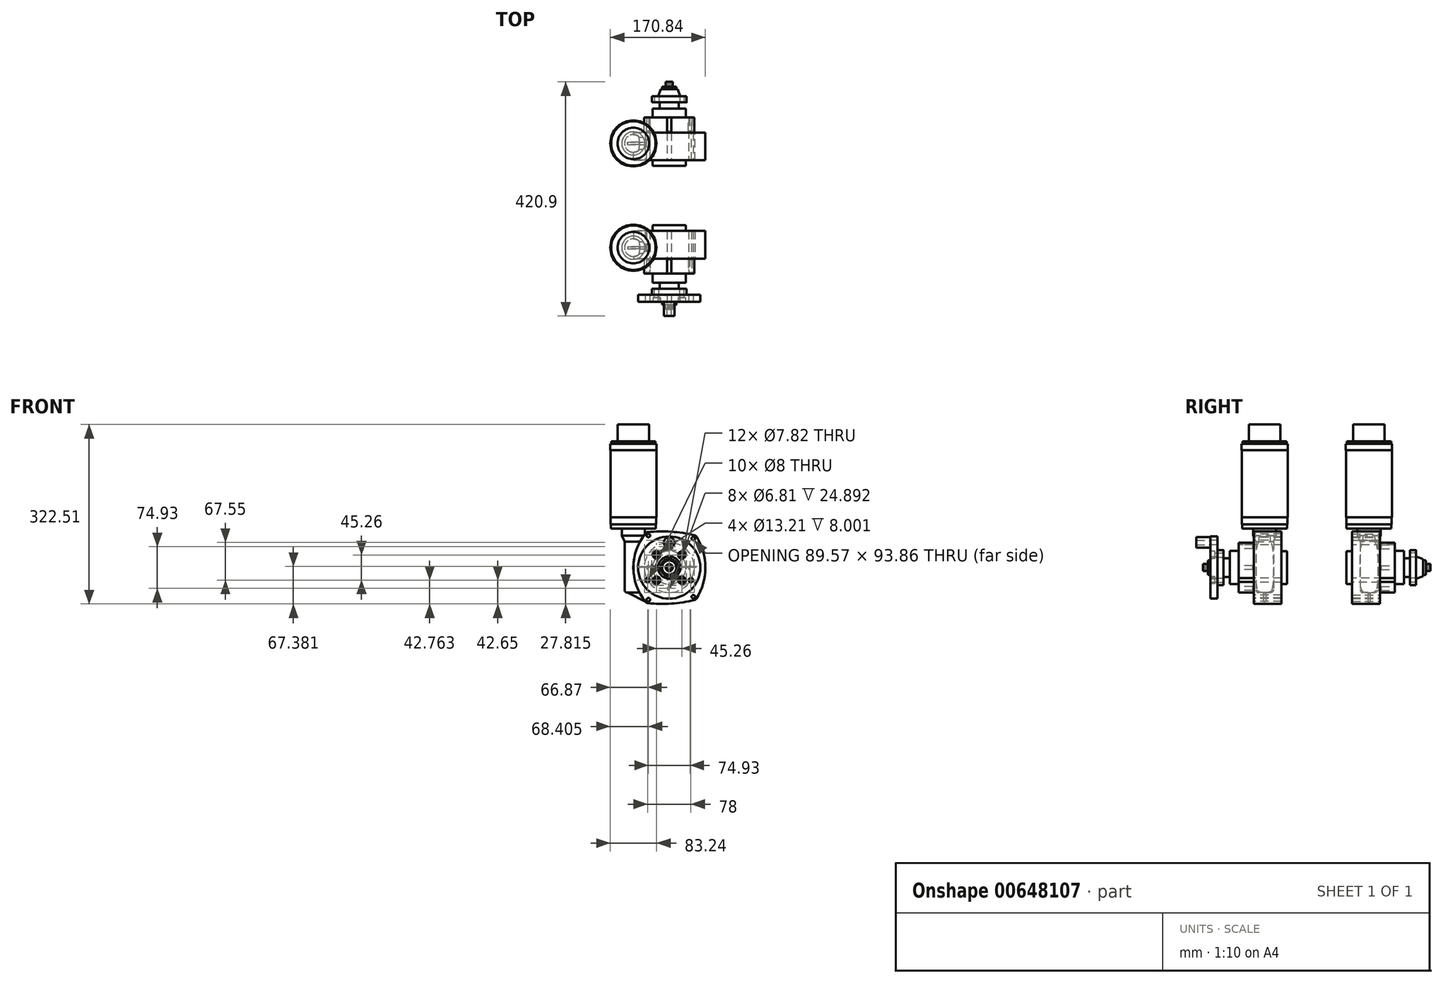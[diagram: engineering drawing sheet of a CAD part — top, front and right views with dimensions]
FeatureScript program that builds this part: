
annotation { "Feature Type Name" : "Feature", "Feature Type Description" : "" }
export const myFeature = defineFeature(function(context is Context, id is Id, definition is map)
    precondition{}
    {
        {
            var Q0;
            Q0=qCreatedBy(makeId("Front.planeOp"),FACE);
            var sketch = newSketch(context, id + "F0", { "sketchPlane" : qUnion([Q0])});
            skCircle(sketch, "E0", {"center": v(0, 0) * mm, "radius": 29.84 * mm});
            skSolve(sketch);
        }
        {
            var Q0;
            Q0 = qSketchRegion(id + "F0", true);
            extrude(context, id + "F1", {"entities" : qUnion([Q0]), "depth" : 16.13 * mm, "offsetDistance" : 25.4 * mm});
        }
        {
            var Q0;
            Q0=makeQuery(id+"F1.opExtrude","CAP_FACE",FACE,{"disambiguationData":[OSD([sQuery(id+"F0.wireOp",EDGE,"E0")])],"isStart":false});
            var sketch = newSketch(context, id + "F2", { "sketchPlane" : qUnion([Q0])});
            skCircle(sketch, "E1", {"center": v(0, 0) * mm, "radius": 44.83 * mm});
            skSolve(sketch);
        }
        {
            var Q0;
            Q0 = qSketchRegion(id + "F2", true);
            extrude(context, id + "F3", {"entities" : qUnion([Q0]), "operationType" : NewBodyOperationType.ADD, "depth" : 27.1 * mm, "offsetDistance" : 25.4 * mm});
        }
        {
            var Q0;
            Q0=makeQuery(id+"F3.opExtrude","CAP_FACE",FACE,{"disambiguationData":[OSD([sQuery(id+"F2.wireOp",EDGE,"E1")])],"isStart":true});
            var sketch = newSketch(context, id + "F4", { "sketchPlane" : qUnion([Q0])});
            skCircle(sketch, "E2", {"center": v(0, 37.47) * mm, "radius": 3.4 * mm});
            skCircle(sketch, "E3.1.0", {"center": v(-37.47, 0) * mm, "radius": 3.4 * mm});
            skCircle(sketch, "E3.2.0", {"center": v(0, -37.47) * mm, "radius": 3.4 * mm});
            skCircle(sketch, "E3.3.0", {"center": v(37.47, 0) * mm, "radius": 3.4 * mm});
            skPoint(sketch, "E3.center", {"position": v(0, 0) * mm});
            skSolve(sketch);
        }
        {
            var Q0;
            Q0 = qSketchRegion(id + "F4", true);
            extrude(context, id + "F5", {"entities" : qUnion([Q0]), "operationType" : NewBodyOperationType.REMOVE, "oppositeDirection" : true, "depth" : 24.9 * mm, "offsetDistance" : 25.4 * mm});
        }
        {
            var Q0;
            Q0=makeQuery(id+"F3.opExtrude","CAP_FACE",FACE,{"disambiguationData":[OSD([sQuery(id+"F2.wireOp",EDGE,"E1")])],"isStart":false});
            var sketch = newSketch(context, id + "F6", { "sketchPlane" : qUnion([Q0])});
            skCircle(sketch, "E4.0", {"center": v(0, 0) * mm, "radius": 44.83 * mm, "construction": true});
            skCircle(sketch, "E5", {"center": v(43.42, -52.43) * mm, "radius": 3.18 * mm});
            skCircle(sketch, "E6", {"center": v(43.42, 52.43) * mm, "radius": 3.18 * mm});
            skLineSegment(sketch, "E7", {"start": v(43.42, -52.43) * mm, "end": v(43.42, 52.43) * mm, "construction": true});
            skCircle(sketch, "E8", {"center": v(-37.44, 57.66) * mm, "radius": 3.18 * mm});
            skCircle(sketch, "E9", {"center": v(-37.44, -57.66) * mm, "radius": 3.18 * mm});
            skLineSegment(sketch, "E10", {"start": v(43.42, 52.43) * mm, "end": v(-37.44, 57.66) * mm, "construction": true});
            skLineSegment(sketch, "E11", {"start": v(-37.44, 57.66) * mm, "end": v(-37.44, -57.66) * mm, "construction": true});
            skLineSegment(sketch, "E12", {"start": v(0, 0) * mm, "end": v(47.8, 57.7) * mm, "construction": true});
            skLineSegment(sketch, "E13", {"start": v(0, 0) * mm, "end": v(-41.17, 63.4) * mm, "construction": true});
            skLineSegment(sketch, "E14", {"start": v(0, 0) * mm, "end": v(47.8, -57.7) * mm, "construction": true});
            skLineSegment(sketch, "E15", {"start": v(0, 0) * mm, "end": v(-41.17, -63.4) * mm, "construction": true});
            skArc(sketch, "E16", {"start": v(49.19, -55.51) * mm, "mid": v(64.97, -0.03) * mm, "end": v(49.22, 55.46) * mm});
            skArc(sketch, "E17", {"start": v(-42.88, 61.34) * mm, "mid": v(-64.47, -0.03) * mm, "end": v(-42.84, -61.4) * mm});
            skArc(sketch, "E18", {"start": v(45.26, 58.31) * mm, "mid": v(3.57, 64.45) * mm, "end": v(-38.56, 63.69) * mm});
            skArc(sketch, "E19", {"start": v(-38.62, -63.72) * mm, "mid": v(3.6, -64.8) * mm, "end": v(45.32, -58.34) * mm});
            skPoint(sketch, "E20.visualSharp", {"position": v(47.8, 57.7) * mm});
            skArc(sketch, "E20.filletArc", {"start": v(49.22, 55.46) * mm, "mid": v(47.52, 57.28) * mm, "end": v(45.26, 58.31) * mm});
            skPoint(sketch, "E21.visualSharp", {"position": v(47.8, -57.7) * mm});
            skArc(sketch, "E21.filletArc", {"start": v(45.32, -58.34) * mm, "mid": v(47.53, -57.3) * mm, "end": v(49.19, -55.51) * mm});
            skPoint(sketch, "E22.visualSharp", {"position": v(-41.17, -63.4) * mm});
            skArc(sketch, "E22.filletArc", {"start": v(-42.84, -61.4) * mm, "mid": v(-40.96, -62.97) * mm, "end": v(-38.62, -63.72) * mm});
            skPoint(sketch, "E23.visualSharp", {"position": v(-41.17, 63.4) * mm});
            skArc(sketch, "E23.filletArc", {"start": v(-38.56, 63.69) * mm, "mid": v(-40.95, 62.95) * mm, "end": v(-42.88, 61.34) * mm});
            skSolve(sketch);
        }
        {
            var Q0;
            Q0 = qSketchRegion(id + "F6", true);
            extrude(context, id + "F7", {"entities" : qUnion([Q0]), "operationType" : NewBodyOperationType.ADD, "depth" : 49.9 * mm, "offsetDistance" : 25.4 * mm});
        }
        {
            var Q0;
            Q0=makeQuery(id+"F7.opExtrude","CAP_FACE",FACE,{"disambiguationData":[OSD([sQuery(id+"F6.wireOp",EDGE,"E5"),sQuery(id+"F6.wireOp",EDGE,"E6"),sQuery(id+"F6.wireOp",EDGE,"E8"),sQuery(id+"F6.wireOp",EDGE,"E9"),sQuery(id+"F6.wireOp",EDGE,"E16"),sQuery(id+"F6.wireOp",EDGE,"E17"),sQuery(id+"F6.wireOp",EDGE,"E18"),sQuery(id+"F6.wireOp",EDGE,"E19"),sQuery(id+"F6.wireOp",EDGE,"E20.filletArc"),sQuery(id+"F6.wireOp",EDGE,"E21.filletArc"),sQuery(id+"F6.wireOp",EDGE,"E22.filletArc"),sQuery(id+"F6.wireOp",EDGE,"E23.filletArc")])],"isStart":false});
            var sketch = newSketch(context, id + "F8", { "sketchPlane" : qUnion([Q0])});
            skCircle(sketch, "E24", {"center": v(0, 0) * mm, "radius": 29.76 * mm});
            skSolve(sketch);
        }
        {
            var Q0;
            Q0 = qSketchRegion(id + "F8", true);
            extrude(context, id + "F9", {"entities" : qUnion([Q0]), "operationType" : NewBodyOperationType.ADD, "depth" : 10.08 * mm, "offsetDistance" : 25.4 * mm});
        }
        {
            var Q0;
            Q0=makeQuery(id+"F1.opExtrude","CAP_FACE",FACE,{"disambiguationData":[OSD([sQuery(id+"F0.wireOp",EDGE,"E0")])],"isStart":true});
            var sketch = newSketch(context, id + "F10", { "sketchPlane" : qUnion([Q0])});
            skCircle(sketch, "E25", {"center": v(0, 0) * mm, "radius": 17.02 * mm});
            skSolve(sketch);
        }
        {
            var Q0;
            Q0 = qSketchRegion(id + "F10", true);
            extrude(context, id + "F11", {"entities" : qUnion([Q0]), "operationType" : NewBodyOperationType.ADD, "depth" : 10.92 * mm, "offsetDistance" : 25.4 * mm});
        }
        {
            var Q0;
            Q0=makeQuery(id+"F11.opExtrude","CAP_FACE",FACE,{"disambiguationData":[OSD([sQuery(id+"F10.wireOp",EDGE,"E25")])],"isStart":false});
            var sketch = newSketch(context, id + "F12", { "sketchPlane" : qUnion([Q0])});
            skLineSegment(sketch, "E26.bottom", {"start": v(25.02, -31.37) * mm, "end": v(-25.02, -31.37) * mm});
            skLineSegment(sketch, "E26.top", {"start": v(25.02, 31.37) * mm, "end": v(-25.02, 31.37) * mm});
            skLineSegment(sketch, "E26.left", {"start": v(31.37, -25.02) * mm, "end": v(31.37, 25.02) * mm});
            skLineSegment(sketch, "E26.right", {"start": v(-31.37, -25.02) * mm, "end": v(-31.37, 25.02) * mm});
            skPoint(sketch, "E26.middle", {"position": v(0, 0) * mm});
            skCircle(sketch, "E27", {"center": v(-22.63, 22.63) * mm, "radius": 3.91 * mm});
            skLineSegment(sketch, "E28", {"start": v(-31.37, 31.37) * mm, "end": v(0, 0) * mm, "construction": true});
            skCircle(sketch, "E29.1.0", {"center": v(-22.63, -22.63) * mm, "radius": 3.91 * mm});
            skCircle(sketch, "E29.2.0", {"center": v(22.63, -22.63) * mm, "radius": 3.91 * mm});
            skCircle(sketch, "E29.3.0", {"center": v(22.63, 22.63) * mm, "radius": 3.91 * mm});
            skPoint(sketch, "E30.visualSharp", {"position": v(-31.37, 31.37) * mm});
            skArc(sketch, "E30.filletArc", {"start": v(-25.02, 31.37) * mm, "mid": v(-29.5, 29.5) * mm, "end": v(-31.37, 25.02) * mm});
            skPoint(sketch, "E31.visualSharp", {"position": v(-31.37, -31.37) * mm});
            skArc(sketch, "E31.filletArc", {"start": v(-31.37, -25.02) * mm, "mid": v(-29.5, -29.5) * mm, "end": v(-25.02, -31.37) * mm});
            skPoint(sketch, "E32.visualSharp", {"position": v(31.37, -31.37) * mm});
            skArc(sketch, "E32.filletArc", {"start": v(25.02, -31.37) * mm, "mid": v(29.5, -29.5) * mm, "end": v(31.37, -25.02) * mm});
            skPoint(sketch, "E33.visualSharp", {"position": v(31.37, 31.37) * mm});
            skArc(sketch, "E33.filletArc", {"start": v(31.37, 25.02) * mm, "mid": v(29.5, 29.5) * mm, "end": v(25.02, 31.37) * mm});
            skSolve(sketch);
        }
        {
            var Q0;
            Q0 = qSketchRegion(id + "F12", true);
            extrude(context, id + "F13", {"entities" : qUnion([Q0]), "operationType" : NewBodyOperationType.ADD, "depth" : 10.92 * mm, "offsetDistance" : 25.4 * mm});
        }
        {
            var Q0;
            Q0=makeQuery(id+"F13.opExtrude","CAP_FACE",FACE,{"disambiguationData":[OSD([sQuery(id+"F12.wireOp",EDGE,"E26.bottom"),sQuery(id+"F12.wireOp",EDGE,"E26.top"),sQuery(id+"F12.wireOp",EDGE,"E26.left"),sQuery(id+"F12.wireOp",EDGE,"E26.right"),sQuery(id+"F12.wireOp",EDGE,"E27"),sQuery(id+"F12.wireOp",EDGE,"E29.1.0"),sQuery(id+"F12.wireOp",EDGE,"E29.2.0"),sQuery(id+"F12.wireOp",EDGE,"E29.3.0"),sQuery(id+"F12.wireOp",EDGE,"E30.filletArc"),sQuery(id+"F12.wireOp",EDGE,"E31.filletArc"),sQuery(id+"F12.wireOp",EDGE,"E32.filletArc"),sQuery(id+"F12.wireOp",EDGE,"E33.filletArc")])],"isStart":false});
            var sketch = newSketch(context, id + "F14", { "sketchPlane" : qUnion([Q0])});
            skCircle(sketch, "E34", {"center": v(0, 0) * mm, "radius": 19.94 * mm});
            skSolve(sketch);
        }
        {
            var Q0;
            Q0 = qSketchRegion(id + "F14", true);
            extrude(context, id + "F15", {"entities" : qUnion([Q0]), "operationType" : NewBodyOperationType.ADD, "depth" : 12.57 * mm, "offsetDistance" : 25.4 * mm, "hasDraft" : true, "draftAngle" : 20 * degree, "draftPullDirection" : true});
        }
        {
            var Q0;
            Q0=makeQuery(id+"F15.opExtrude","CAP_FACE",FACE,{"disambiguationData":[OSD([sQuery(id+"F14.wireOp",EDGE,"E34")])],"isStart":false});
            var sketch = newSketch(context, id + "F16", { "sketchPlane" : qUnion([Q0])});
            skCircle(sketch, "E35", {"center": v(0, 0) * mm, "radius": 12.95 * mm});
            skSolve(sketch);
        }
        {
            var Q0;
            Q0 = qSketchRegion(id + "F16", true);
            extrude(context, id + "F17", {"entities" : qUnion([Q0]), "operationType" : NewBodyOperationType.ADD, "depth" : 4.9 * mm, "offsetDistance" : 25.4 * mm});
        }
        {
            var Q0;
            Q0=makeQuery(id+"F17.opExtrude","CAP_FACE",FACE,{"disambiguationData":[OSD([sQuery(id+"F16.wireOp",EDGE,"E35")])],"isStart":false});
            var sketch = newSketch(context, id + "F18", { "sketchPlane" : qUnion([Q0])});
            skCircle(sketch, "E36", {"center": v(0, 0) * mm, "radius": 6.35 * mm});
            skSolve(sketch);
        }
        {
            var Q0;
            Q0 = qSketchRegion(id + "F18", true);
            extrude(context, id + "F19", {"entities" : qUnion([Q0]), "operationType" : NewBodyOperationType.ADD, "depth" : 8.38 * mm, "offsetDistance" : 25.4 * mm});
        }
        {
            var Q0;
            Q0=makeQuery(id+"F19.opExtrude","CAP_FACE",FACE,{"disambiguationData":[OSD([sQuery(id+"F18.wireOp",EDGE,"E36")])],"isStart":false});
            var sketch = newSketch(context, id + "F20", { "sketchPlane" : qUnion([Q0])});
            skCircle(sketch, "E37.cCircle", {"center": v(0, 0) * mm, "radius": 4 * mm, "construction": true});
            skLineSegment(sketch, "E37.0", {"start": v(3.84, -2.02) * mm, "end": v(1.28, -4.14) * mm});
            skLineSegment(sketch, "E37.1", {"start": v(1.28, -4.14) * mm, "end": v(-2.02, -3.84) * mm});
            skLineSegment(sketch, "E37.2", {"start": v(-2.02, -3.84) * mm, "end": v(-4.14, -1.28) * mm});
            skLineSegment(sketch, "E37.3", {"start": v(-4.14, -1.28) * mm, "end": v(-3.84, 2.02) * mm});
            skLineSegment(sketch, "E37.4", {"start": v(-3.84, 2.02) * mm, "end": v(-1.28, 4.14) * mm});
            skLineSegment(sketch, "E37.5", {"start": v(-1.28, 4.14) * mm, "end": v(2.02, 3.84) * mm});
            skLineSegment(sketch, "E37.6", {"start": v(2.02, 3.84) * mm, "end": v(4.14, 1.28) * mm});
            skLineSegment(sketch, "E37.7", {"start": v(4.14, 1.28) * mm, "end": v(3.84, -2.02) * mm});
            skPoint(sketch, "E37.0.midPoint", {"position": v(2.56, -3.08) * mm});
            skSolve(sketch);
        }
        {
            var Q0;
            Q0 = qSketchRegion(id + "F20", true);
            extrude(context, id + "F21", {"entities" : qUnion([Q0]), "operationType" : NewBodyOperationType.REMOVE, "oppositeDirection" : true, "depth" : 5.08 * mm, "offsetDistance" : 25.4 * mm});
        }
        {
            var Q0;
            Q0=qCreatedBy(makeId("Top.planeOp"),FACE);
            cPlane(context, id + "F22", {"entities" : qUnion([Q0]), "cplaneType" : CPlaneType.OFFSET, "offset" : 44.96 * mm, "oppositeDirection" : true, "width" : 152.4 * mm, "height" : 152.4 * mm});
        }
        {
            var Q0;
            Q0=qCreatedBy(id+"F22.planeOp",FACE);
            var sketch = newSketch(context, id + "F23", { "sketchPlane" : qUnion([Q0])});
            skCircle(sketch, "E38", {"center": v(-64.47, -62.93) * mm, "radius": 15.88 * mm});
            skLineSegment(sketch, "E39", {"start": v(-64.47, -93.13) * mm, "end": v(-64.47, -43.24) * mm, "construction": true});
            skSolve(sketch);
        }
        {
            var Q0;
            Q0 = qSketchRegion(id + "F23", true);
            extrude(context, id + "F24", {"entities" : qUnion([Q0]), "operationType" : NewBodyOperationType.ADD, "depth" : 91.7 * mm, "offsetDistance" : 25.4 * mm});
        }
        {
            var Q0;
            Q0=makeQuery(id+"F24.opExtrude","CAP_EDGE",EDGE,{"disambiguationData":[OSD([sQuery(id+"F23.wireOp",EDGE,"E38")])],"isStart":true});
            fillet(context, id + "F25", {"entities" : qUnion([Q0]), "radius" : 5.08 * mm, "tangentPropagation" : true, "allowEdgeOverflow" : false});
        }
        {
            var Q0;
            {var subQ0=sQuery(id+"F23.wireOp",EDGE,"E38");Q0=makeQuery(id+"F25.opFillet","BLEND_EDGE",EDGE,{"blendedFrom":[makeQuery(id+"F24.opExtrude","CAP_EDGE",EDGE,{"disambiguationData":[OSD([subQ0])],"isStart":true}),makeQuery(id+"F24.opExtrude","SWEPT_FACE",FACE,{"disambiguationData":[OSD([subQ0])]})],"blendedInto":[makeQuery(id+"F24.opExtrude","SWEPT_FACE",FACE,{"disambiguationData":[OSD([subQ0])]})]});}
            cPoint(context, id + "F26", {"entities" : qUnion([Q0]), "parameter" : 0.5});
        }
        {
            var Q0;
            Q0=qCreatedBy(makeId("Front.planeOp"),FACE);
            var Q1;
            Q1 = qCreatedBy(id + "F26" ,VERTEX);
            cPlane(context, id + "F27", {"entities" : qUnion([Q0, Q1]), "cplaneType" : CPlaneType.PLANE_POINT, "offset" : 25.4 * mm, "width" : 152.4 * mm, "height" : 152.4 * mm});
        }
        {
            var Q0;
            Q0=qCreatedBy(id+"F27.planeOp",FACE);
            var sketch = newSketch(context, id + "F28", { "sketchPlane" : qUnion([Q0])});
            skLineSegment(sketch, "E40.0", {"start": v(-53.67, -44.96) * mm, "end": v(-75.26, -44.96) * mm});
            skLineSegment(sketch, "E41", {"start": v(-75.26, -44.96) * mm, "end": v(-42.84, -61.4) * mm});
            skLineSegment(sketch, "E42", {"start": v(-53.67, -44.96) * mm, "end": v(-42.84, -61.4) * mm});
            skSolve(sketch);
        }
        {
            var Q0;
            Q0 = qSketchRegion(id + "F28", true);
            extrude(context, id + "F29", {"entities" : qUnion([Q0]), "operationType" : NewBodyOperationType.ADD, "depth" : 2.03 * mm, "offsetDistance" : 25.4 * mm, "hasSecondDirection" : true, "secondDirectionOppositeDirection" : true, "secondDirectionDepth" : 2.03 * mm});
        }
        {
            var Q0;
            Q0=makeQuery(id+"F24.opExtrude","CAP_FACE",FACE,{"disambiguationData":[OSD([sQuery(id+"F23.wireOp",EDGE,"E38")])],"isStart":false});
            var sketch = newSketch(context, id + "F30", { "sketchPlane" : qUnion([Q0])});
            skCircle(sketch, "E43", {"center": v(-64.47, -62.93) * mm, "radius": 15.88 * mm});
            skSolve(sketch);
        }
        {
            var Q0;
            Q0 = qSketchRegion(id + "F30", true);
            extrude(context, id + "F31", {"entities" : qUnion([Q0]), "operationType" : NewBodyOperationType.ADD, "depth" : 10.6 * mm, "offsetDistance" : 25.4 * mm, "hasDraft" : true, "draftAngle" : 25 * degree});
        }
        {
            var Q0;
            Q0=makeQuery(id+"F31.opExtrude","CAP_FACE",FACE,{"disambiguationData":[OSD([sQuery(id+"F30.wireOp",EDGE,"E43")])],"isStart":false});
            var sketch = newSketch(context, id + "F32", { "sketchPlane" : qUnion([Q0])});
            skCircle(sketch, "E44", {"center": v(-64.47, -62.93) * mm, "radius": 20.81 * mm});
            skSolve(sketch);
        }
        {
            var Q0;
            Q0 = qSketchRegion(id + "F32", true);
            extrude(context, id + "F33", {"entities" : qUnion([Q0]), "operationType" : NewBodyOperationType.ADD, "depth" : 12.7 * mm, "offsetDistance" : 25.4 * mm});
        }
        {
            var Q0;
            Q0=makeQuery(id+"F33.opExtrude","CAP_FACE",FACE,{"disambiguationData":[OSD([sQuery(id+"F32.wireOp",EDGE,"E44")])],"isStart":false});
            var sketch = newSketch(context, id + "F34", { "sketchPlane" : qUnion([Q0])});
            skCircle(sketch, "E45", {"center": v(-64.47, -62.93) * mm, "radius": 40.26 * mm});
            skSolve(sketch);
        }
        {
            var Q0;
            Q0 = qSketchRegion(id + "F34", true);
            extrude(context, id + "F35", {"entities" : qUnion([Q0]), "operationType" : NewBodyOperationType.ADD, "depth" : 7.62 * mm, "offsetDistance" : 25.4 * mm});
        }
        {
            var Q0;
            Q0=makeQuery(id+"F35.opExtrude","CAP_FACE",FACE,{"disambiguationData":[OSD([sQuery(id+"F34.wireOp",EDGE,"E45")])],"isStart":false});
            var sketch = newSketch(context, id + "F36", { "sketchPlane" : qUnion([Q0])});
            skCircle(sketch, "E46", {"center": v(-64.47, -62.93) * mm, "radius": 40.77 * mm});
            skSolve(sketch);
        }
        {
            var Q0;
            Q0 = qSketchRegion(id + "F36", true);
            extrude(context, id + "F37", {"entities" : qUnion([Q0]), "operationType" : NewBodyOperationType.ADD, "depth" : 12.7 * mm, "offsetDistance" : 25.4 * mm});
        }
        {
            var Q0;
            Q0=makeQuery(id+"F37.opExtrude","CAP_FACE",FACE,{"disambiguationData":[OSD([sQuery(id+"F36.wireOp",EDGE,"E46")])],"isStart":false});
            var sketch = newSketch(context, id + "F38", { "sketchPlane" : qUnion([Q0])});
            skCircle(sketch, "E47", {"center": v(-64.47, -62.93) * mm, "radius": 41.28 * mm});
            skSolve(sketch);
        }
        {
            var Q0;
            Q0 = qSketchRegion(id + "F38", true);
            extrude(context, id + "F39", {"entities" : qUnion([Q0]), "operationType" : NewBodyOperationType.ADD, "depth" : 120.9 * mm, "offsetDistance" : 25.4 * mm});
        }
        {
            var Q0;
            Q0=makeQuery(id+"F39.opExtrude","CAP_FACE",FACE,{"disambiguationData":[OSD([sQuery(id+"F38.wireOp",EDGE,"E47")])],"isStart":false});
            var sketch = newSketch(context, id + "F40", { "sketchPlane" : qUnion([Q0])});
            skCircle(sketch, "E48", {"center": v(-64.47, -62.93) * mm, "radius": 41.4 * mm});
            skSolve(sketch);
        }
        {
            var Q0;
            Q0 = qSketchRegion(id + "F40", true);
            extrude(context, id + "F41", {"entities" : qUnion([Q0]), "operationType" : NewBodyOperationType.ADD, "depth" : 11.43 * mm, "offsetDistance" : 25.4 * mm});
        }
        {
            var Q0;
            Q0=makeQuery(id+"F41.opExtrude","CAP_FACE",FACE,{"disambiguationData":[OSD([sQuery(id+"F40.wireOp",EDGE,"E48")])],"isStart":false});
            var sketch = newSketch(context, id + "F42", { "sketchPlane" : qUnion([Q0])});
            skCircle(sketch, "E49", {"center": v(-64.47, -62.93) * mm, "radius": 39.93 * mm});
            skSolve(sketch);
        }
        {
            var Q0;
            Q0 = qSketchRegion(id + "F42", true);
            extrude(context, id + "F43", {"entities" : qUnion([Q0]), "operationType" : NewBodyOperationType.ADD, "depth" : 4.06 * mm, "offsetDistance" : 25.4 * mm});
        }
        {
            var Q0;
            Q0=makeQuery(id+"F43.opExtrude","CAP_FACE",FACE,{"disambiguationData":[OSD([sQuery(id+"F42.wireOp",EDGE,"E49")])],"isStart":false});
            var sketch = newSketch(context, id + "F44", { "sketchPlane" : qUnion([Q0])});
            skCircle(sketch, "E50", {"center": v(-64.47, -62.93) * mm, "radius": 28.32 * mm});
            skSolve(sketch);
        }
        {
            var Q0;
            Q0 = qSketchRegion(id + "F44", true);
            extrude(context, id + "F45", {"entities" : qUnion([Q0]), "operationType" : NewBodyOperationType.ADD, "depth" : 30.48 * mm, "offsetDistance" : 25.4 * mm});
        }
        {
            var Q0;
            Q0=makeQuery(id+"F1.opExtrude","SWEPT_BODY",BODY,{"disambiguationData":[OSD([sQuery(id+"F0.wireOp",EDGE,"E0")])]});
            var Q1;
            Q1=makeQuery(id+"F7.opExtrude","CAP_FACE",FACE,{"disambiguationData":[OSD([sQuery(id+"F6.wireOp",EDGE,"E5"),sQuery(id+"F6.wireOp",EDGE,"E6"),sQuery(id+"F6.wireOp",EDGE,"E8"),sQuery(id+"F6.wireOp",EDGE,"E9"),sQuery(id+"F6.wireOp",EDGE,"E16"),sQuery(id+"F6.wireOp",EDGE,"E17"),sQuery(id+"F6.wireOp",EDGE,"E18"),sQuery(id+"F6.wireOp",EDGE,"E19"),sQuery(id+"F6.wireOp",EDGE,"E20.filletArc"),sQuery(id+"F6.wireOp",EDGE,"E21.filletArc"),sQuery(id+"F6.wireOp",EDGE,"E22.filletArc"),sQuery(id+"F6.wireOp",EDGE,"E23.filletArc")])],"isStart":false});
            mirror(context, id + "F46", {"entities" : qUnion([Q0]), "mirrorPlane" : qUnion([Q1])});
        }
        {
            var Q0;
            Q0=makeQuery(id+"F46.opPattern","COPY",BODY,{"derivedFrom":makeQuery(id+"F1.opExtrude","SWEPT_BODY",BODY,{"disambiguationData":[OSD([sQuery(id+"F0.wireOp",EDGE,"E0")])]}),"instanceName":"1"});
            var Q1;
            Q1=makeQuery(id+"F46.opPattern","COPY",EDGE,{"derivedFrom":makeQuery(id+"F7.opExtrude","SWEPT_EDGE",EDGE,{"disambiguationData":[OSD([sQuery(id+"F6.wireOp",EDGE,"E16"),sQuery(id+"F6.wireOp",EDGE,"E20.filletArc")])]}),"instanceName":"1"});
            transform(context, id + "F47", {"entities" : qUnion([Q0]), "transformType" : TransformType.TRANSLATION_DISTANCE, "transformDirection" : qUnion([Q1]), "distance" : 127 * mm, "makeCopy" : false});
        }
        {
            var Q0;
            Q0=makeQuery(id+"F46.opPattern","COPY",FACE,{"derivedFrom":makeQuery(id+"F13.opExtrude","CAP_FACE",FACE,{"disambiguationData":[OSD([sQuery(id+"F12.wireOp",EDGE,"E26.bottom"),sQuery(id+"F12.wireOp",EDGE,"E26.top"),sQuery(id+"F12.wireOp",EDGE,"E26.left"),sQuery(id+"F12.wireOp",EDGE,"E26.right"),sQuery(id+"F12.wireOp",EDGE,"E27"),sQuery(id+"F12.wireOp",EDGE,"E29.1.0"),sQuery(id+"F12.wireOp",EDGE,"E29.2.0"),sQuery(id+"F12.wireOp",EDGE,"E29.3.0"),sQuery(id+"F12.wireOp",EDGE,"E30.filletArc"),sQuery(id+"F12.wireOp",EDGE,"E31.filletArc"),sQuery(id+"F12.wireOp",EDGE,"E32.filletArc"),sQuery(id+"F12.wireOp",EDGE,"E33.filletArc")])],"isStart":false}),"instanceName":"1"});
            var sketch = newSketch(context, id + "F48", { "sketchPlane" : qUnion([Q0])});
            skCircle(sketch, "E51.0", {"center": v(0, 0) * mm, "radius": 19.94 * mm});
            skCircle(sketch, "E52", {"center": v(0, 0) * mm, "radius": 55.88 * mm});
            skCircle(sketch, "E53.0", {"center": v(22.63, 22.63) * mm, "radius": 3.91 * mm});
            skCircle(sketch, "E54.0", {"center": v(-22.63, 22.63) * mm, "radius": 3.91 * mm});
            skCircle(sketch, "E55.0", {"center": v(-22.63, -22.63) * mm, "radius": 3.91 * mm});
            skCircle(sketch, "E56.0", {"center": v(22.63, -22.63) * mm, "radius": 3.91 * mm});
            skSolve(sketch);
        }
        {
            var Q0;
            Q0 = qSketchRegion(id + "F48", true);
            extrude(context, id + "F49", {"entities" : qUnion([Q0]), "depth" : 12.7 * mm, "offsetDistance" : 25.4 * mm});
        }
        {
            var Q0;
            Q0=makeQuery(id+"F49.opExtrude","CAP_FACE",FACE,{"disambiguationData":[OSD([sQuery(id+"F48.wireOp",EDGE,"E51.0"),sQuery(id+"F48.wireOp",EDGE,"E52"),sQuery(id+"F48.wireOp",EDGE,"E53.0"),sQuery(id+"F48.wireOp",EDGE,"E54.0"),sQuery(id+"F48.wireOp",EDGE,"E55.0"),sQuery(id+"F48.wireOp",EDGE,"E56.0")])],"isStart":false});
            var sketch = newSketch(context, id + "F50", { "sketchPlane" : qUnion([Q0])});
            skCircle(sketch, "E57", {"center": v(0, 45.03) * mm, "radius": 4 * mm});
            skCircle(sketch, "E58.1.0", {"center": v(-39, -22.52) * mm, "radius": 4 * mm});
            skCircle(sketch, "E58.2.0", {"center": v(39, -22.52) * mm, "radius": 4 * mm});
            skPoint(sketch, "E58.center", {"position": v(0, 0) * mm});
            skSolve(sketch);
        }
        {
            var Q0;
            Q0 = qSketchRegion(id + "F50", true);
            extrude(context, id + "F51", {"entities" : qUnion([Q0]), "operationType" : NewBodyOperationType.REMOVE, "endBound" : BoundingType.THROUGH_ALL, "oppositeDirection" : true, "depth" : 25.4 * mm, "offsetDistance" : 25.4 * mm});
        }
        {
            var Q0;
            Q0=makeQuery(id+"F49.opExtrude","CAP_FACE",FACE,{"disambiguationData":[OSD([sQuery(id+"F48.wireOp",EDGE,"E51.0"),sQuery(id+"F48.wireOp",EDGE,"E52"),sQuery(id+"F48.wireOp",EDGE,"E53.0"),sQuery(id+"F48.wireOp",EDGE,"E54.0"),sQuery(id+"F48.wireOp",EDGE,"E55.0"),sQuery(id+"F48.wireOp",EDGE,"E56.0")])],"isStart":false});
            var sketch = newSketch(context, id + "F52", { "sketchPlane" : qUnion([Q0])});
            skCircle(sketch, "E59", {"center": v(-22.63, 22.63) * mm, "radius": 6.6 * mm});
            skCircle(sketch, "E60", {"center": v(22.63, 22.63) * mm, "radius": 6.6 * mm});
            skCircle(sketch, "E61", {"center": v(22.63, -22.63) * mm, "radius": 6.6 * mm});
            skCircle(sketch, "E62", {"center": v(-22.63, -22.63) * mm, "radius": 6.6 * mm});
            skSolve(sketch);
        }
        {
            var Q0;
            Q0 = qSketchRegion(id + "F52", true);
            extrude(context, id + "F53", {"entities" : qUnion([Q0]), "operationType" : NewBodyOperationType.REMOVE, "oppositeDirection" : true, "depth" : 8 * mm, "offsetDistance" : 25.4 * mm});
        }
        {
            var Q0;
            Q0=makeQuery(id+"F49.opExtrude","CAP_FACE",FACE,{"disambiguationData":[OSD([sQuery(id+"F48.wireOp",EDGE,"E51.0"),sQuery(id+"F48.wireOp",EDGE,"E52"),sQuery(id+"F48.wireOp",EDGE,"E53.0"),sQuery(id+"F48.wireOp",EDGE,"E54.0"),sQuery(id+"F48.wireOp",EDGE,"E55.0"),sQuery(id+"F48.wireOp",EDGE,"E56.0")])],"isStart":false});
            var sketch = newSketch(context, id + "F54", { "sketchPlane" : qUnion([Q0])});
            skCircle(sketch, "E63.0", {"center": v(0, 45.03) * mm, "radius": 4 * mm});
            skCircle(sketch, "E64", {"center": v(0, 45.03) * mm, "radius": 9.53 * mm});
            skSolve(sketch);
        }
        {
            var Q0;
            Q0 = qSketchRegion(id + "F54", true);
            extrude(context, id + "F55", {"entities" : qUnion([Q0]), "depth" : 25.4 * mm, "offsetDistance" : 25.4 * mm});
        }
    });
